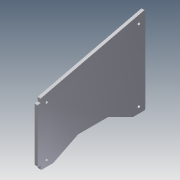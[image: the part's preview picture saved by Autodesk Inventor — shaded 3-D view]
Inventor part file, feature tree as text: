
AUTODESK INVENTOR PART (.ipt)
format: ipt  version: 2014 (Build 180170000, 170)  size: 144,896 bytes
history: native  units: mm
features: extrude x5, sketch x5, fillet x1
ambient origin geometry x8: Origin, YZ Plane, XZ Plane, XY Plane, X Axis, Y Axis, Z Axis, Center Point
bodies: Solid1 (feature_tree)
feature tree (11):
  extrude  "Extrusion1"  Depth=210.0mm
  extrude  "Extrusion2"  Depth=25.0mm
  extrude  "Extrusion3"  Depth=6.0mm TaperAngle=0.0deg
  extrude  "Extrusion4"  Depth=3.0mm TaperAngle=0.0deg
  extrude  "Extrusion5"  Depth=8.1mm
  fillet  "Fillet1"  Radius=6.0mm
  sketch  "Sketch1"  dims[d0=150.0mm d1=210.0mm]
  sketch  "Sketch2"  dims[d2=6.0mm d3=0.0mm d4=25.0mm]
  sketch  "Sketch3"  dims[d5=50.0mm d6=6.0mm d7=0.0mm]
  sketch  "Sketch4"  dims[d8=50.0mm d9=3.0mm d10=0.0mm]
  sketch  "Sketch5"  dims[d11=8.1mm d12=8.1mm d13=6.0mm d14=6.0mm d15=0.0mm d16=2.0mm d17=12.5mm d18=12.5mm d19=12.5mm d21=5.4mm d22=12.5mm d23=6.0mm d24=0.0mm]
